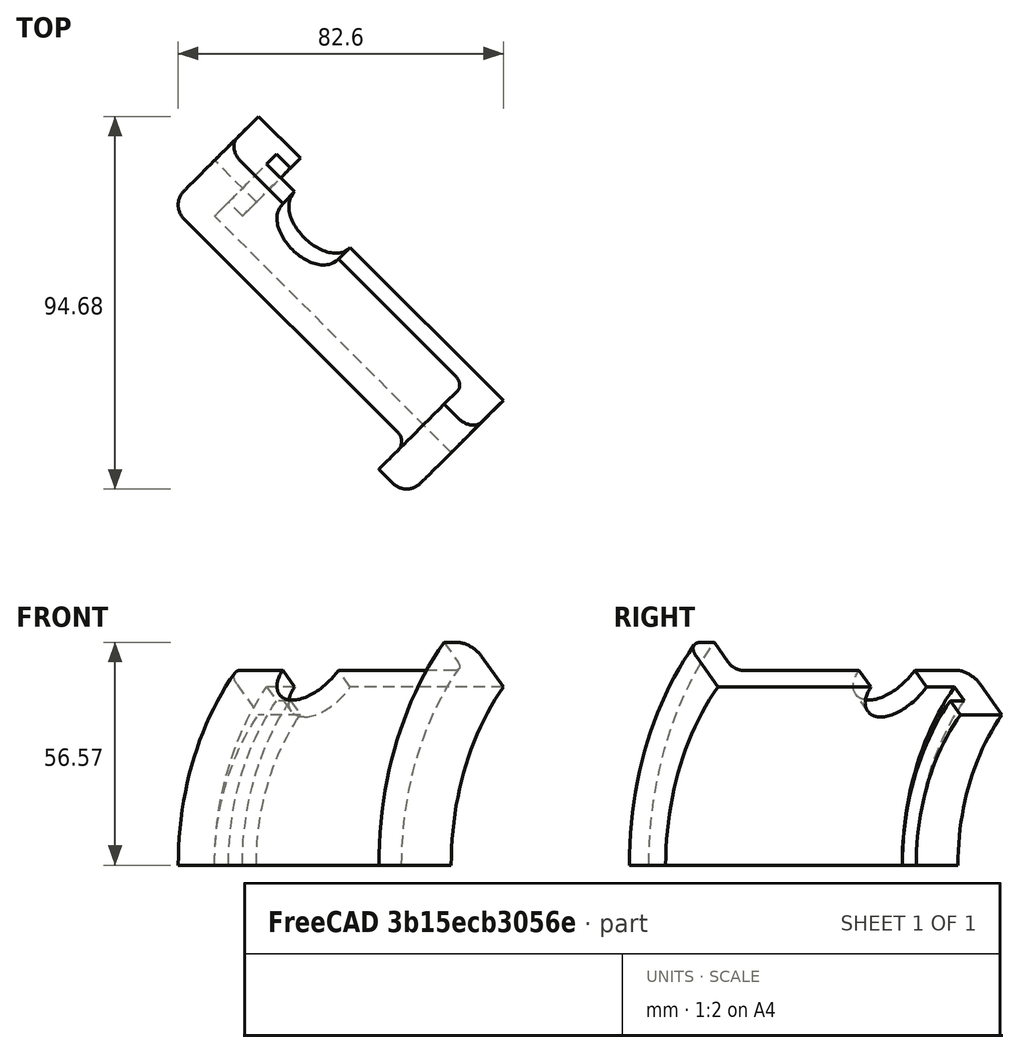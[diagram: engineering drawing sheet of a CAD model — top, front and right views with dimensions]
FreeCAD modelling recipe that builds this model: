
FCSTD DOCUMENT  (FreeCAD 0.15R4671 (Git))
Label: sphere_support_cyls4_w5
License: All rights reserved
LicenseURL: http://en.wikipedia.org/wiki/All_rights_reserved
objects: Part::Cut×11, Part::Box×8, Part::Cylinder×6, Part::Fillet×3, Part::MultiFuse×2
note: 30 computed .brp shape members not serialized (recipe doc carries the construction recipe); baked Part::Feature solids carry a one-line shape summary decoded from their .brp

FEATURE [Part::Cylinder] Cylinder  label="Base_Cylinder"
  Angle = 360
  Height = 10
  Radius = 80
FEATURE [Part::Cylinder] Cylinder001  label="Body_Cylinder"
  Angle = 360
  Height = 90
  Placement = pos=(0,0,5) rot=(0,0,1;0rad)
  Radius = 70
FEATURE [Part::MultiFuse] Fusion  label="Core_Fusion"
  Shapes = -> [Cylinder,Cylinder001]
FEATURE [Part::Cylinder] Cylinder002  label="Inner_Hole"
  Angle = 360
  Height = 85
  Radius = 64
FEATURE [Part::Cut] Cut
  Base = -> Fusion
  Tool = -> Cylinder002
FEATURE [Part::Cylinder] Cylinder003  label="Inner_Lip"
  Angle = 360
  Height = 10
  Placement = pos=(0,0,80) rot=(0,0,1;0rad)
  Radius = 59
FEATURE [Part::MultiFuse] Fusion001
  Shapes = -> [Cut,Cylinder003]
FEATURE [Part::Cylinder] Cylinder004  label="Through_Hole"
  Angle = 360
  Height = 100
  Radius = 54
FEATURE [Part::Cut] Cut001
  Base = -> Fusion001
  Tool = -> Cylinder004
FEATURE [Part::Fillet] Fillet
  Base = -> Cut001
  Edges = 1 edges r=3: [Edge12]
FEATURE [Part::Fillet] Fillet001
  Base = -> Fillet
  Edges = 1 edges r=5: [Edge11]
FEATURE [Part::Fillet] Fillet002
  Base = -> Fillet001
  Edges = 1 edges r=5: [Edge13]
FEATURE [Part::Cylinder] Cylinder005  label="Bearing_Holes"
  Angle = 360
  Height = 180
  Placement = pos=(0,90,65) rot=(1,0,0;1.5708rad)
  Radius = 10
FEATURE [Part::Cut] Cut002
  Base = -> Fillet002
  Tool = -> Cylinder005
FEATURE [Part::Box] Box  label="Bearing_Slot"
  Height = 35
  Length = 20
  Placement = pos=(-10,48,65) rot=(0,0,1;0rad)
  Width = 25
FEATURE [Part::Cut] Cut003
  Base = -> Cut002
  Tool = -> Box
FEATURE [Part::Box] Box001  label="Cube"
  Height = 35
  Length = 10
  Placement = pos=(0,48,65) rot=(0,1,0;0.261799rad)
  Width = 25
FEATURE [Part::Cut] Cut004
  Base = -> Cut003
  Tool = -> Box001
FEATURE [Part::Box] Box002  label="Cube001"
  Height = 35
  Length = 10
  Placement = pos=(-9.95,48,64) rot=(0,-1,0;0.261799rad)
  Width = 25
FEATURE [Part::Cut] Cut005
  Base = -> Cut004
  Tool = -> Box002
FEATURE [Part::Box] Box003  label="Tab_Cut_R"
  Height = 80
  Length = 20
  Placement = pos=(63,-10,20) rot=(0,0,1;0rad)
  Width = 20
FEATURE [Part::Cut] Cut006
  Base = -> Cut005
  Tool = -> Box003
FEATURE [Part::Box] Box004  label="Tab_Cut_L"
  Height = 80
  Length = 20
  Placement = pos=(-83,-10,20) rot=(0,0,1;0rad)
  Width = 20
FEATURE [Part::Cut] Cut007
  Base = -> Cut006
  Tool = -> Box004
FEATURE [Part::Box] Box005  label="Cube002"
  Height = 100
  Length = 100
  Placement = pos=(0,0,0) rot=(0,0,-1;1.5708rad)
  Width = 100
FEATURE [Part::Cut] Cut008
  Base = -> Cut007
  Tool = -> Box005
FEATURE [Part::Box] Box006  label="Cube003"
  Height = 100
  Length = 200
  Placement = pos=(-71,-71,0) rot=(0,0,1;0.785398rad)
  Width = 100
FEATURE [Part::Cut] Cut009
  Base = -> Cut008
  Placement = pos=(0,0,0) rot=(-0.707107,-0.707107,0;1.5708rad)
  Tool = -> Box006
FEATURE [Part::Box] Box007  label="Cube004"
  Height = 100
  Length = 100
  Placement = pos=(0,0,0) rot=(0,0,1;0.785398rad)
  Width = 100
FEATURE [Part::Cut] Cut010
  Base = -> Cut009
  Tool = -> Box007
